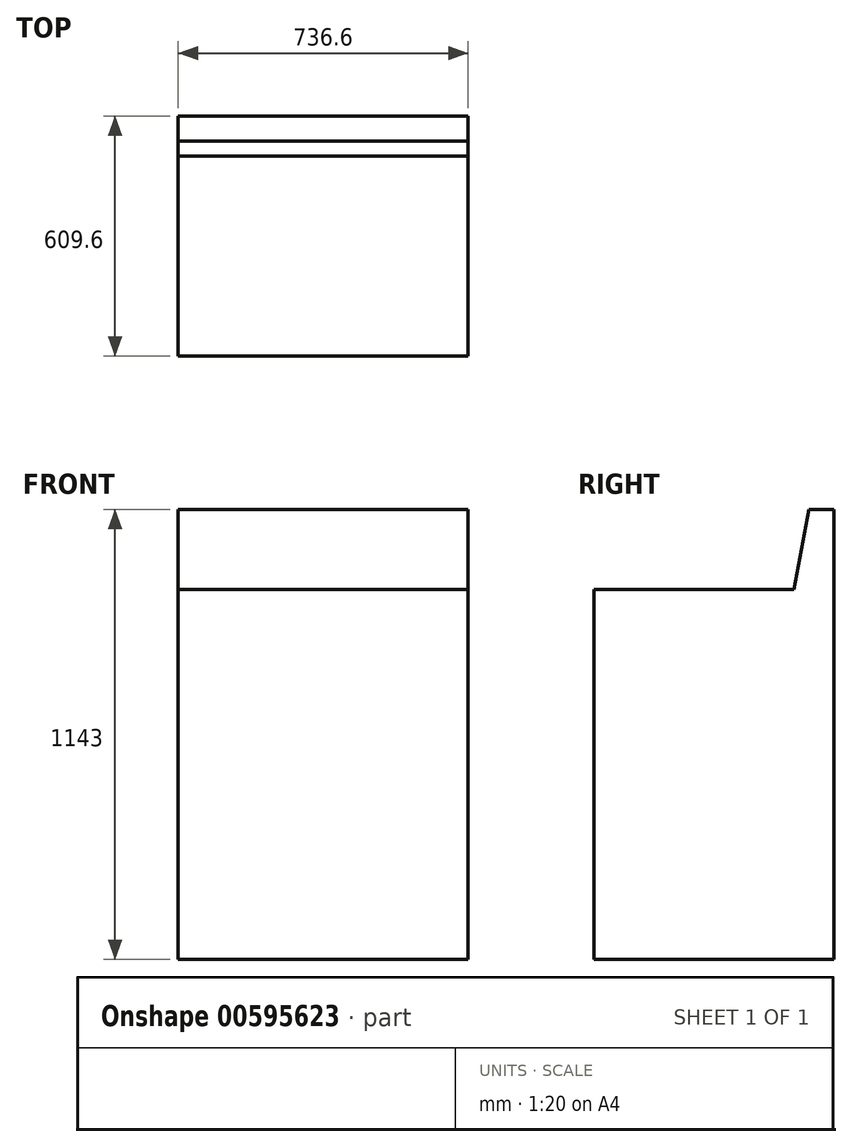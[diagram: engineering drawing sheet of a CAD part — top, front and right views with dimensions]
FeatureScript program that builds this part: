
annotation { "Feature Type Name" : "Feature", "Feature Type Description" : "" }
export const myFeature = defineFeature(function(context is Context, id is Id, definition is map)
    precondition{}
    {
        {
            var Q0;
            Q0=qCreatedBy(makeId("Right.planeOp"),FACE);
            var sketch = newSketch(context, id + "F0", { "sketchPlane" : qUnion([Q0])});
            skLineSegment(sketch, "E0.bottom", {"start": v(0, 0) * mm, "end": v(609.6, 0) * mm});
            skLineSegment(sketch, "E0.top", {"start": v(0, 939.8) * mm, "end": v(609.6, 939.8) * mm});
            skLineSegment(sketch, "E0.left", {"start": v(0, 0) * mm, "end": v(0, 939.8) * mm});
            skLineSegment(sketch, "E0.right", {"start": v(609.6, 0) * mm, "end": v(609.6, 939.8) * mm});
            skLineSegment(sketch, "E1.bottom", {"start": v(609.6, 939.8) * mm, "end": v(508, 939.8) * mm});
            skLineSegment(sketch, "E1.top", {"start": v(609.6, 1143) * mm, "end": v(546.1, 1143) * mm});
            skLineSegment(sketch, "E1.left", {"start": v(609.6, 939.8) * mm, "end": v(609.6, 1143) * mm});
            skLineSegment(sketch, "E2", {"start": v(508, 939.8) * mm, "end": v(546.1, 1143) * mm});
            skSolve(sketch);
        }
        {
            var Q0;
            Q0=qSketchRegion(id+"F0",true);
            extrude(context, id + "F1", {"entities" : qUnion([Q0]), "depth" : 736.6 * mm, "offsetDistance" : 25.4 * mm});
        }
    });
